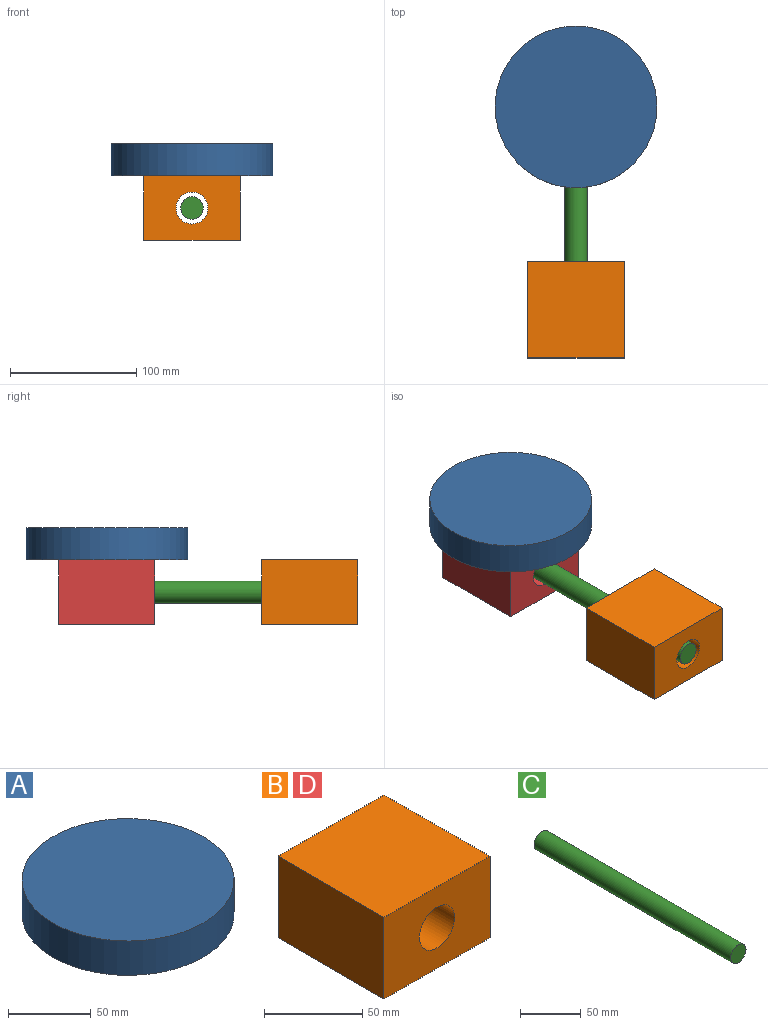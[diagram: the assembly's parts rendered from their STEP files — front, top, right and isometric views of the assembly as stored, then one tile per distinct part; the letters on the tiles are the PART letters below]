
ASSEMBLY  parts=4 mates=3
PART A: 3 faces, bbox 128.4x128.4x25.4 mm
  f0: cylinder r=64.19mm len=128.39mm, axis (0,0,-1), area 10244.8mm2, adj f1,f2
  f1: plane 128.39x128.39mm, normal (0,0,1), area 12945.9mm2, adj f0
  f2: plane 128.39x128.39mm, normal (0,0,-1), area 12945.9mm2, adj f0
PART B: 7 faces, bbox 76.2x76.2x50.8 mm
  f0: plane 76.2x76.2mm, normal (0,0,1), area 5806.4mm2, adj f1,f3,f4,f5
  f1: plane 76.2x50.8mm, normal (-1,0,0), area 3871mm2, adj f0,f2,f4,f5
  f2: plane 76.2x76.2mm, normal (0,0,-1), area 5806.4mm2, adj f1,f3,f4,f5
  f3: plane 76.2x50.8mm, normal (1,0,0), area 3871mm2, adj f0,f2,f4,f5
  f4: plane 76.2x50.8mm, normal (0,-1,0), area 3364.3mm2, adj f0,f1,f2,f3,f6
  f5: plane 76.2x50.8mm, normal (0,1,0), area 3364.3mm2, adj f0,f1,f2,f3,f6
  f6: cylinder r=12.7mm len=76.2mm, axis (0,-1,0), area 6080.5mm2, adj f4,f5
PART C: 3 faces, bbox 17.8x228.6x17.8 mm
  f0: cylinder r=8.89mm len=228.6mm, axis (0,1,0), area 12769mm2, adj f1,f2
  f1: plane 17.78x17.78mm, normal (0,-1,0), area 248.3mm2, adj f0
  f2: plane 17.78x17.78mm, normal (0,1,0), area 248.3mm2, adj f0
PART D: same geometry as B
PLACE A rot(axis=(0.71,0.71,0),180deg) t=(43.29,15.39,23.45)mm
PLACE B t=(36.67,-107.54,-44.76)mm
PLACE C t=(188.92,44.86,-80.06)mm
PLACE D t=(36.67,53.49,-44.76)mm
MATE fastened B.f6 <-> C.f0  axis (0,-1,0) through (43.29,-183.74,-27.35)mm
MATE slider C.f0 <-> D.f6  axis (0,1,0) through (43.29,44.86,-27.35)mm
MATE fastened A.f0 <-> D.f0  axis (0,0,-1) through (43.29,15.39,-1.95)mm
